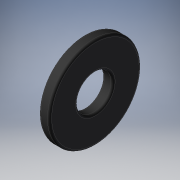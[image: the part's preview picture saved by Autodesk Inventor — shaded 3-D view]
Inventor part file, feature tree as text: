
AUTODESK INVENTOR PART (.ipt)
format: ipt  version: 2019 (Build 230136000, 136)  size: 171,520 bytes
history: native  units: mm
features: other x7, revolve x1, sketch x1
ambient origin geometry x8: Origin, YZ Plane, XZ Plane, XY Plane, X Axis, Y Axis, Z Axis, Center Point
bodies: Solid1 (feature_tree)
feature tree (9):
  revolve  "Revolution1"  [1 undecoded]
  other  "SW_HW_XY"
  other  "SW_HW_YZ"
  other  "SW_HW_ZX"
  other  "SW_HW_X"
  other  "SW_HW_Y"
  other  "SW_HW_Z"
  other  "SW_HW_Center"
  sketch  "Sketch_1"  dims[d0=360.0deg]
note: 1 required parameter value undecoded (feature->parameter linkage not recoverable at this tier; creation-order binding heuristic only, values carry confidence <= 0.55)
